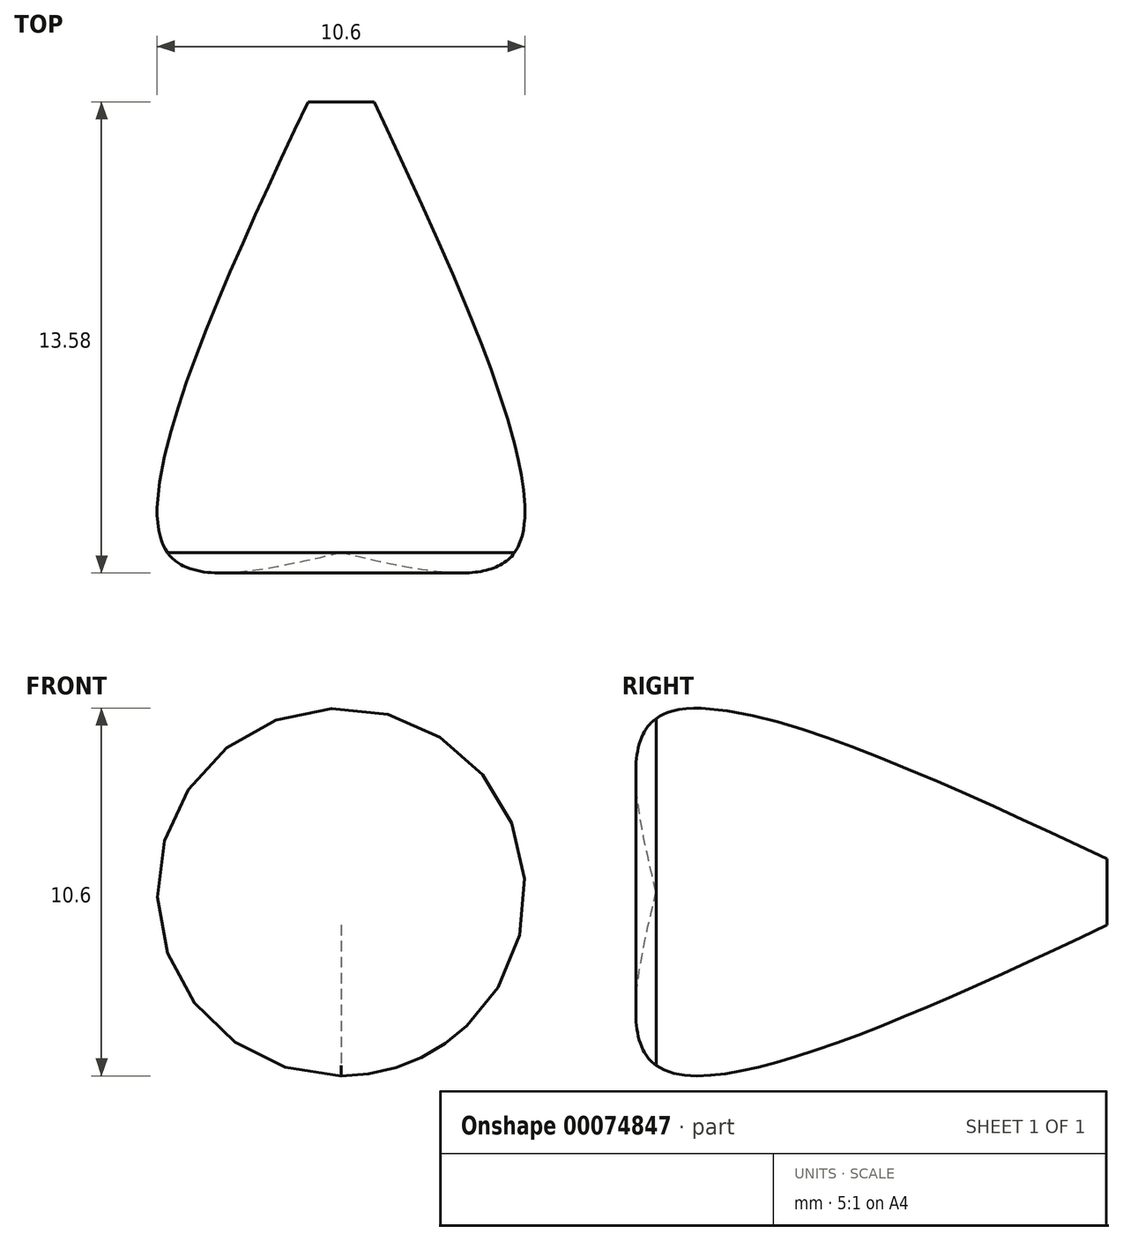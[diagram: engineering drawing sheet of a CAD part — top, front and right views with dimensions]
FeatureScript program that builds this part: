
annotation { "Feature Type Name" : "Feature", "Feature Type Description" : "" }
export const myFeature = defineFeature(function(context is Context, id is Id, definition is map)
    precondition{}
    {
        {
            var Q0;
            Q0=qCreatedBy(makeId("Top.planeOp"),FACE);
            var sketch = newSketch(context, id + "F0", { "sketchPlane" : qUnion([Q0])});
            skLineSegment(sketch, "E0", {"start": v(0, 0) * mm, "end": v(0, 12.79) * mm});
            skLineSegment(sketch, "E1", {"start": v(0, 0) * mm, "end": v(5, 0) * mm});
            skFitSpline(sketch, "E2", {"points": [v(0, 15) * mm, v(5, 0) * mm, v(0, 0) * mm], "startDerivative": vector(14.76, -30.94) * mm, "endDerivative": vector(-17.8, 4.22) * mm});
            skArc(sketch, "E3.filletArc", {"start": v(0.95, 13) * mm, "mid": v(0.4, 13.27) * mm, "end": v(0, 12.79) * mm});
            skSolve(sketch);
        }
        {
            var Q0;
            Q0=makeQuery(id+"F0.imprint","IMPRINT",FACE,{"disambiguationData":[TD([[makeQuery(id+"F0.imprint","IMPRINT",EDGE,{"derivedFrom":sQuery(id+"F0.wireOp",EDGE,"E0")}),-1.0]])]});
            var Q1;
            {var subQ0=sQuery(id+"F0.wireOp",EDGE,"E1");Q1=makeQuery(id+"F0.imprint","IMPRINT",FACE,{"disambiguationData":[TD([[makeQuery(id+"F0.imprint","IMPRINT",EDGE,{"derivedFrom":subQ0}),-1.0]])]});}
            var Q2;
            Q2=sQuery(id+"F0.wireOp",EDGE,"E0");
            revolve(context, id + "F1", {"entities" : qUnion([Q0, Q1]), "axis" : qUnion([Q2]), "revolveType" : RevolveType.FULL});
        }
    });
